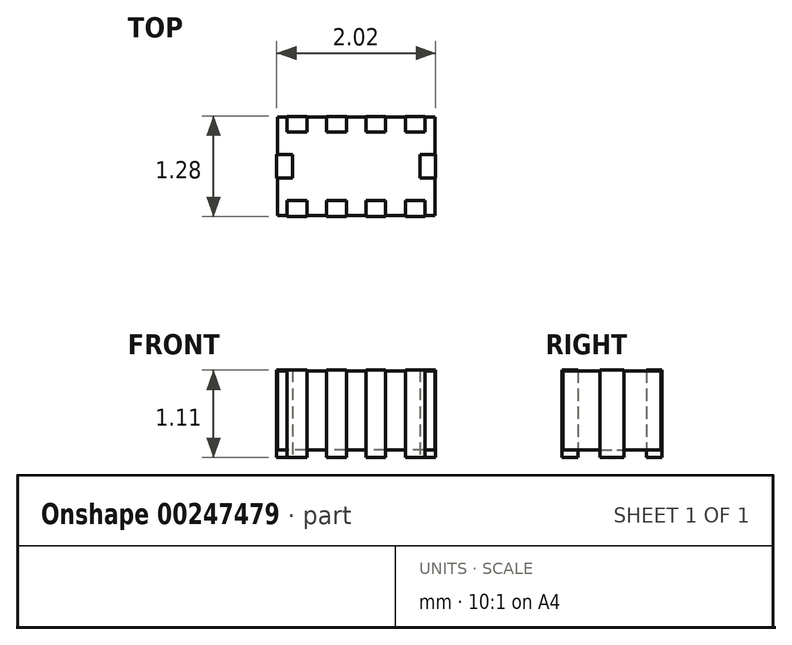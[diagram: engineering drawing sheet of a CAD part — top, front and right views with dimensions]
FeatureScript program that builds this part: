
annotation { "Feature Type Name" : "Feature", "Feature Type Description" : "" }
export const myFeature = defineFeature(function(context is Context, id is Id, definition is map)
    precondition{}
    {
        {
            var Q0;
            Q0=qCreatedBy(makeId("Top.planeOp"),FACE);
            var sketch = newSketch(context, id + "F0", { "sketchPlane" : qUnion([Q0])});
            skLineSegment(sketch, "E0.bottom", {"start": v(1, -0.63) * mm, "end": v(-1, -0.63) * mm});
            skLineSegment(sketch, "E0.top", {"start": v(1, 0.63) * mm, "end": v(-1, 0.62) * mm});
            skLineSegment(sketch, "E0.left", {"start": v(1, -0.63) * mm, "end": v(1, 0.63) * mm});
            skLineSegment(sketch, "E0.right", {"start": v(-1, -0.63) * mm, "end": v(-1, 0.62) * mm});
            skPoint(sketch, "E0.middle", {"position": v(0, 0) * mm});
            skSolve(sketch);
        }
        {
            var Q0;
            Q0=qSketchRegion(id+"F0",true);
            extrude(context, id + "F1", {"entities" : qUnion([Q0]), "depth" : 1 * mm});
        }
        {
            var Q0;
            Q0=qCreatedBy(makeId("Top.planeOp"),FACE);
            var sketch = newSketch(context, id + "F2", { "sketchPlane" : qUnion([Q0])});
            skLineSegment(sketch, "E1.bottom", {"start": v(-0.87, -0.44) * mm, "end": v(-0.62, -0.44) * mm});
            skLineSegment(sketch, "E1.top", {"start": v(-0.87, -0.64) * mm, "end": v(-0.62, -0.64) * mm});
            skLineSegment(sketch, "E1.left", {"start": v(-0.87, -0.44) * mm, "end": v(-0.87, -0.64) * mm});
            skLineSegment(sketch, "E1.right", {"start": v(-0.62, -0.44) * mm, "end": v(-0.62, -0.64) * mm});
            skLineSegment(sketch, "E2", {"start": v(-1.03, 0) * mm, "end": v(1, 0) * mm, "construction": true});
            skLineSegment(sketch, "E3", {"start": v(0, 0.62) * mm, "end": v(0, -0.33) * mm, "construction": true});
            skLineSegment(sketch, "E4.bottom", {"start": v(-0.37, -0.44) * mm, "end": v(-0.12, -0.44) * mm});
            skLineSegment(sketch, "E4.top", {"start": v(-0.37, -0.64) * mm, "end": v(-0.12, -0.64) * mm});
            skLineSegment(sketch, "E4.left", {"start": v(-0.37, -0.44) * mm, "end": v(-0.37, -0.64) * mm});
            skLineSegment(sketch, "E4.right", {"start": v(-0.12, -0.44) * mm, "end": v(-0.12, -0.64) * mm});
            skLineSegment(sketch, "E5.MirrorCS", {"start": v(0.37, -0.64) * mm, "end": v(0.12, -0.64) * mm});
            skLineSegment(sketch, "E6.MirrorCS", {"start": v(0.37, -0.44) * mm, "end": v(0.37, -0.64) * mm});
            skLineSegment(sketch, "E7.MirrorCS", {"start": v(0.12, -0.44) * mm, "end": v(0.12, -0.64) * mm});
            skLineSegment(sketch, "E8.MirrorCS", {"start": v(0.37, -0.44) * mm, "end": v(0.12, -0.44) * mm});
            skLineSegment(sketch, "E9.MirrorCS", {"start": v(0.87, -0.44) * mm, "end": v(0.62, -0.44) * mm});
            skLineSegment(sketch, "E10.MirrorCS", {"start": v(0.87, -0.64) * mm, "end": v(0.62, -0.64) * mm});
            skLineSegment(sketch, "E11.MirrorCS", {"start": v(0.87, -0.44) * mm, "end": v(0.87, -0.64) * mm});
            skLineSegment(sketch, "E12.MirrorCS", {"start": v(0.62, -0.44) * mm, "end": v(0.62, -0.64) * mm});
            skLineSegment(sketch, "E13.MirrorCS", {"start": v(0, -0.62) * mm, "end": v(0, 0.33) * mm, "construction": true});
            skLineSegment(sketch, "E14.MirrorCS", {"start": v(-0.37, 0.44) * mm, "end": v(-0.12, 0.44) * mm});
            skLineSegment(sketch, "E15.MirrorCS", {"start": v(-0.62, 0.44) * mm, "end": v(-0.62, 0.64) * mm});
            skLineSegment(sketch, "E16.MirrorCS", {"start": v(-0.87, 0.44) * mm, "end": v(-0.87, 0.64) * mm});
            skLineSegment(sketch, "E17.MirrorCS", {"start": v(-0.87, 0.64) * mm, "end": v(-0.62, 0.64) * mm});
            skLineSegment(sketch, "E18.MirrorCS", {"start": v(-0.87, 0.44) * mm, "end": v(-0.62, 0.44) * mm});
            skLineSegment(sketch, "E19.MirrorCS", {"start": v(0.87, 0.64) * mm, "end": v(0.62, 0.64) * mm});
            skLineSegment(sketch, "E20.MirrorCS", {"start": v(0.87, 0.44) * mm, "end": v(0.62, 0.44) * mm});
            skLineSegment(sketch, "E21.MirrorCS", {"start": v(0.37, 0.44) * mm, "end": v(0.12, 0.44) * mm});
            skLineSegment(sketch, "E22.MirrorCS", {"start": v(0.62, 0.44) * mm, "end": v(0.62, 0.64) * mm});
            skLineSegment(sketch, "E23.MirrorCS", {"start": v(0.87, 0.44) * mm, "end": v(0.87, 0.64) * mm});
            skLineSegment(sketch, "E24.MirrorCS", {"start": v(-0.37, 0.64) * mm, "end": v(-0.12, 0.64) * mm});
            skLineSegment(sketch, "E25.MirrorCS", {"start": v(0.12, 0.44) * mm, "end": v(0.12, 0.64) * mm});
            skLineSegment(sketch, "E26.MirrorCS", {"start": v(0.37, 0.44) * mm, "end": v(0.37, 0.64) * mm});
            skLineSegment(sketch, "E27.MirrorCS", {"start": v(0.37, 0.64) * mm, "end": v(0.12, 0.64) * mm});
            skLineSegment(sketch, "E28.MirrorCS", {"start": v(-0.12, 0.44) * mm, "end": v(-0.12, 0.64) * mm});
            skLineSegment(sketch, "E29.MirrorCS", {"start": v(-0.37, 0.44) * mm, "end": v(-0.37, 0.64) * mm});
            skLineSegment(sketch, "E30.bottom", {"start": v(-1.01, 0.15) * mm, "end": v(-0.81, 0.15) * mm});
            skLineSegment(sketch, "E30.top", {"start": v(-1.01, -0.15) * mm, "end": v(-0.81, -0.15) * mm});
            skLineSegment(sketch, "E30.left", {"start": v(-1.01, 0.15) * mm, "end": v(-1.01, -0.15) * mm});
            skLineSegment(sketch, "E30.right", {"start": v(-0.81, 0.15) * mm, "end": v(-0.81, -0.15) * mm});
            skLineSegment(sketch, "E31.MirrorCS", {"start": v(1.01, 0.15) * mm, "end": v(0.81, 0.15) * mm});
            skLineSegment(sketch, "E32.MirrorCS", {"start": v(0.81, 0.15) * mm, "end": v(0.81, -0.15) * mm});
            skLineSegment(sketch, "E33.MirrorCS", {"start": v(1.01, -0.15) * mm, "end": v(0.81, -0.15) * mm});
            skLineSegment(sketch, "E34.MirrorCS", {"start": v(1.01, 0.15) * mm, "end": v(1.01, -0.15) * mm});
            skSolve(sketch);
        }
        {
            var Q0;
            Q0=qSketchRegion(id+"F2",true);
            extrude(context, id + "F3", {"entities" : qUnion([Q0]), "depth" : 1.01 * mm, "hasSecondDirection" : true, "secondDirectionOppositeDirection" : true, "secondDirectionDepth" : .1 * mm});
        }
    });
